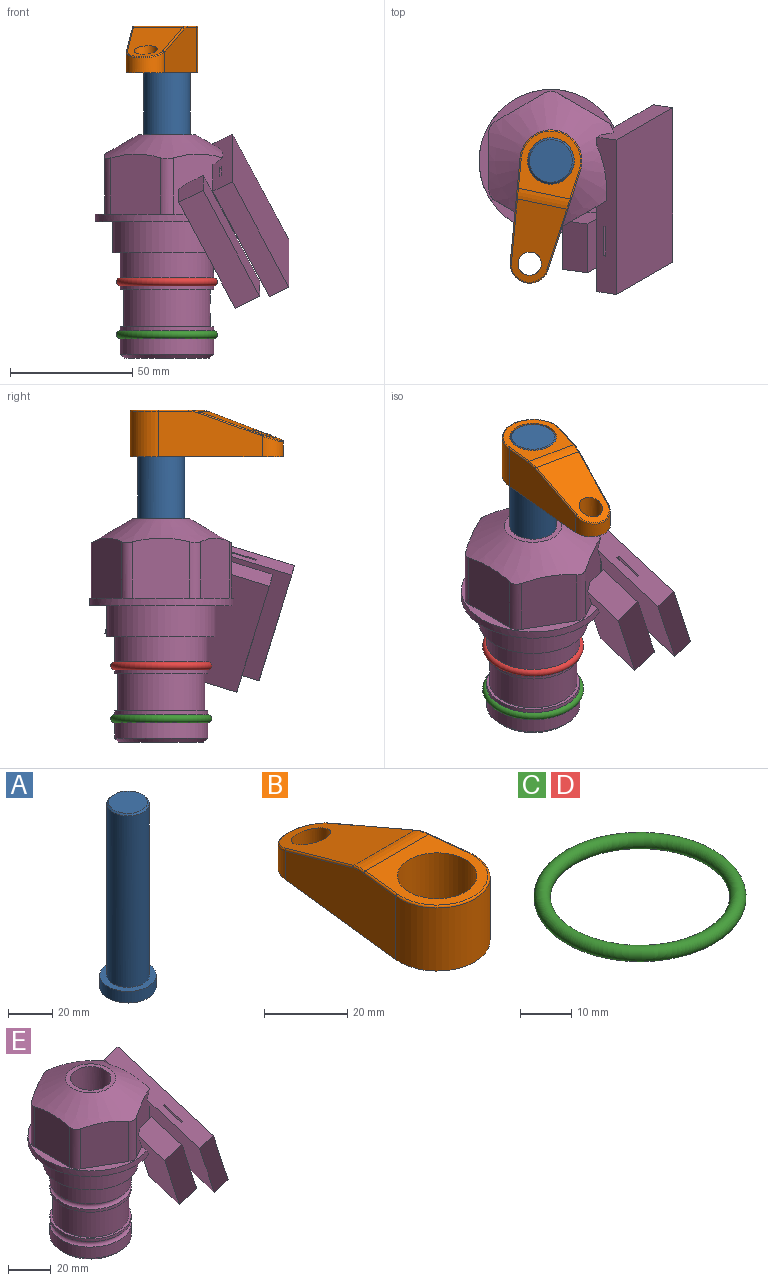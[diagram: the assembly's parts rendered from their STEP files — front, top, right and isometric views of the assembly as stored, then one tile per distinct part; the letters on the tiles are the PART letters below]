
ASSEMBLY  parts=5 mates=3
PART A: 6 faces, bbox 25.4x25.4x101.6 mm
  f0: plane 17.46x17.46mm, normal (0,0,1), area 239.5mm2, adj f5
  f1: plane 25.4x25.4mm, normal (0,0,-1), area 506.7mm2, adj f2
  f2: cylinder r=12.7mm len=25.4mm, axis (0,0,1), area 506.7mm2, adj f1,f3
  f3: plane 25.4x25.4mm, normal (0,0,1), area 221.7mm2, adj f2,f4
  f4: cylinder r=9.53mm len=94.46mm, axis (0,0,1), area 5653mm2, adj f3,f5
  f5: cone r=8.73mm half-angle=45deg, axis (0,0,-1), area 64.4mm2, adj f0,f4
PART B: 44 faces, bbox 27.5x64.5x19.1 mm
  f0: plane 2.3x0.95mm, normal (0,0,-1), area 1mm2, adj f25,f30,f34
  f1: plane 63.5x25.4mm, normal (0,0,-1), area 561.7mm2, adj f2,f3,f4,f5,f6,f7,f19,f20
  f2: cylinder r=12.7mm len=25.4mm, axis (0,0,-1), area 792.2mm2, adj f1,f3,f5,f13
  f3: plane 42.33x18.54mm, normal (0.99,0.11,0), area 647mm2, adj f1,f2,f4,f11,f12,f14
  f4: cylinder r=7.94mm len=15.78mm, axis (0,0,-1), area 158.6mm2, adj f1,f3,f5,f16
  f5: plane 42.33x18.54mm, normal (-0.99,0.11,0), area 647mm2, adj f1,f2,f4,f15,f17,f18
  f6: cylinder r=9.53mm len=19.05mm, axis (0,0,-1), area 1140.1mm2, adj f1,f8
  f7: cylinder r=4.76mm len=10.98mm, axis (0,0,-1), area 276.1mm2, adj f1,f9
  f8: plane 25.83x24.38mm, normal (0,0,1), area 262.2mm2, adj f6,f10,f11,f13,f15
  f9: plane 32.49x20.55mm, normal (0,0.34,0.94), area 489.9mm2, adj f7,f10,f14,f16,f18
  f10: cylinder r=12.7mm len=21.49mm, axis (-1,0,0), area 93.2mm2, adj f8,f9,f12,f17
  f11: cylinder r=0.51mm len=12.34mm, axis (0.11,-0.99,0), area 9.9mm2, adj f3,f8,f12,f13
  f12: bspline ~7.62x1.64mm, area 3.5mm2, adj f3,f10,f11,f14
  f13: torus R=12.19mm, axis (0,0,1), area 33.6mm2, adj f2,f8,f11,f15
  f14: cylinder r=0.51mm len=26.01mm, axis (0.1,-0.93,0.34), area 21.6mm2, adj f3,f9,f12,f16
  f15: cylinder r=0.51mm len=12.34mm, axis (0.11,0.99,0), area 9.9mm2, adj f5,f8,f13,f17
  f16: bspline ~15.78x7.05mm, area 15.7mm2, adj f4,f9,f14,f18
  f17: bspline ~7.62x1.64mm, area 3.5mm2, adj f5,f10,f15,f18
  f18: cylinder r=0.51mm len=26.01mm, axis (0.1,0.93,-0.34), area 21.6mm2, adj f5,f9,f16,f17
  f19: plane 21.6x14.29mm, normal (-0.99,-0.11,0), area 242.6mm2, adj f1,f26,f28,f34,f36,f38
  f20: plane 21.6x14.29mm, normal (0.99,-0.11,0), area 242.6mm2, adj f1,f27,f29,f37,f39,f41
  f21: cylinder r=12.7mm len=14.29mm, axis (0,0,-1), area 173.2mm2, adj f1,f26,f27,f30,f31,f33
  f22: cylinder r=7.94mm len=7.63mm, axis (0,0,-1), area 53.8mm2, adj f1,f28,f29,f42
  f23: plane 2.3x0.95mm, normal (0,0,-1), area 1mm2, adj f25,f33,f37
  f24: plane 17.94x12.32mm, normal (0,-0.34,-0.94), area 191.2mm2, adj f25,f38,f41,f42
  f25: cylinder r=9.53mm len=12.93mm, axis (-1,0,0), area 37.5mm2, adj f0,f23,f24,f31,f36,f39
  f26: cylinder r=1.59mm len=14.29mm, axis (0,0,-1), area 49mm2, adj f1,f19,f21,f32
  f27: cylinder r=1.59mm len=14.29mm, axis (0,0,-1), area 49mm2, adj f1,f20,f21,f35
  f28: cylinder r=1.59mm len=7.28mm, axis (0,0,-1), area 22.1mm2, adj f1,f19,f22,f40
  f29: cylinder r=1.59mm len=7.28mm, axis (0,0,-1), area 22.1mm2, adj f1,f20,f22,f43
  f30: torus R=14.29mm, axis (0,0,1), area 5.8mm2, adj f0,f21,f31,f32
  f31: bspline ~11.06x2.73mm, area 20.8mm2, adj f21,f25,f30,f33
  f32: sphere r=1.59mm, area 5.4mm2, adj f26,f30,f34
  f33: torus R=14.29mm, axis (0,0,1), area 5.8mm2, adj f21,f23,f31,f35
  f34: cylinder r=1.59mm len=1.68mm, axis (-0.11,0.99,0), area 2.4mm2, adj f0,f19,f32,f36
  f35: sphere r=1.59mm, area 5.4mm2, adj f27,f33,f37
  f36: bspline ~5.82x2.33mm, area 7.7mm2, adj f19,f25,f34,f38
  f37: cylinder r=1.59mm len=1.68mm, axis (0.11,0.99,0), area 2.4mm2, adj f20,f23,f35,f39
  f38: cylinder r=1.59mm len=18.33mm, axis (0.1,-0.93,0.34), area 46.7mm2, adj f19,f24,f36,f40
  f39: bspline ~5.82x2.33mm, area 7.7mm2, adj f20,f25,f37,f41
  f40: sphere r=1.59mm, area 3.6mm2, adj f28,f38,f42
  f41: cylinder r=1.59mm len=18.33mm, axis (0.1,0.93,-0.34), area 46.7mm2, adj f20,f24,f39,f43
  f42: bspline ~8.31x1.84mm, area 15.3mm2, adj f22,f24,f40,f43
  f43: sphere r=1.59mm, area 3.6mm2, adj f29,f41,f42
PART C: 1 faces, bbox 44.7x44.7x3.2 mm
  f0: torus R=19.05mm, axis (0,0,1), area 1193.9mm2
PART D: same geometry as C
PART E: 54 faces, bbox 79.4x84.1x91.8 mm
  f0: plane 24.5x20.32mm, normal (0.5,-0.87,0), area 480.9mm2, adj f4,f5,f10,f18,f43,f47,f50,f51
  f1: plane 23.46x15.81mm, normal (1,0,0), area 286.3mm2, adj f3,f4,f10,f43
  f2: plane 0.56x0.17mm, normal (1,0,0), area 0mm2, adj f3,f5,f44
  f3: cylinder r=5.08mm len=23.01mm, axis (0,0,-1), area 115.4mm2, adj f1,f2,f5,f10,f14,f43,f44
  f4: cylinder r=5.08mm len=12.46mm, axis (0,0,-1), area 51.3mm2, adj f0,f1,f10,f43
  f5: cone r=11.73mm half-angle=60deg, axis (0,0,-1), area 1947.2mm2, adj f0,f2,f3,f11,f12,f13,f14,f15
  f6: cylinder r=17.78mm len=35.56mm, axis (0,0,1), area 1670.8mm2, adj f24,f25,f32
  f7: cylinder r=19.05mm len=38.1mm, axis (0,0,1), area 1191.9mm2, adj f27,f28,f31
  f8: plane 58.66x58.66mm, normal (0,0,-1), area 1112.1mm2, adj f9,f29,f50,f51
  f9: cylinder r=29.33mm len=58.66mm, axis (0,0,-1), area 544.4mm2, adj f8,f10,f50,f51
  f10: plane 58.66x58.66mm, normal (0,0,1), area 440.8mm2, adj f0,f1,f3,f4,f9,f11,f12,f13
  f11: plane 24.5x20.32mm, normal (-0.5,-0.87,0), area 562.8mm2, adj f5,f10,f17,f18
  f12: plane 24.5x23.48mm, normal (-1,0,0), area 562.8mm2, adj f5,f10,f16,f17
  f13: plane 24.5x20.32mm, normal (-0.5,0.87,0), area 562.8mm2, adj f5,f10,f15,f16
  f14: plane 24.5x20.32mm, normal (0.5,0.87,0), area 562.8mm2, adj f3,f5,f10,f15
  f15: cylinder r=5.08mm len=23.01mm, axis (0,0,-1), area 121.2mm2, adj f5,f10,f13,f14
  f16: cylinder r=5.08mm len=23.01mm, axis (0,0,-1), area 121.2mm2, adj f5,f10,f12,f13
  f17: cylinder r=5.08mm len=23.01mm, axis (0,0,-1), area 121.2mm2, adj f5,f10,f11,f12
  f18: cylinder r=5.08mm len=23.01mm, axis (0,0,-1), area 121.2mm2, adj f0,f5,f10,f11
  f19: plane 23.46x23.46mm, normal (0,0,1), area 147.4mm2, adj f5,f36
  f20: plane 34.93x34.93mm, normal (0,0,-1), area 958mm2, adj f30
  f21: cylinder r=19.05mm len=38.1mm, axis (0,0,1), area 760.1mm2, adj f22,f30
  f22: torus R=19.05mm, axis (0,0,1), area 565.3mm2, adj f21,f23
  f23: cylinder r=19.05mm len=38.1mm, axis (0,0,1), area 190mm2, adj f22,f24
  f24: plane 38.1x38.1mm, normal (0,0,1), area 146.9mm2, adj f6,f23
  f25: plane 38.1x38.1mm, normal (0,0,-1), area 146.9mm2, adj f6,f26
  f26: cylinder r=19.05mm len=38.1mm, axis (0,0,1), area 190mm2, adj f25,f27
  f27: torus R=19.05mm, axis (0,0,1), area 565.3mm2, adj f7,f26
  f28: plane 44.45x44.45mm, normal (0,0,-1), area 411.7mm2, adj f7,f29
  f29: cylinder r=22.23mm len=44.45mm, axis (0,0,1), area 1773.5mm2, adj f8,f28
  f30: cone r=19.05mm half-angle=45deg, axis (0,0,1), area 257.5mm2, adj f20,f21
  f31: cylinder r=3.17mm len=6.75mm, axis (-1,0,0), area 128mm2, adj f7,f34
  f32: cylinder r=3.17mm len=6.35mm, axis (-1,0,0), area 102.5mm2, adj f6,f34
  f33: plane 25.4x25.4mm, normal (0,0,1), area 506.7mm2, adj f34
  f34: cylinder r=12.7mm len=66.42mm, axis (0,0,-1), area 5236.2mm2, adj f31,f32,f33,f35
  f35: cone r=9.53mm half-angle=30deg, axis (0,0,-1), area 443.4mm2, adj f34,f36
  f36: cylinder r=9.53mm len=19.05mm, axis (0,0,-1), area 849mm2, adj f19,f35
  f37: plane 4.41x2.91mm, normal (-0.89,0.13,-0.43), area 6.1mm2, adj f5,f44,f47
  f38: plane 43.62x23.78mm, normal (0,-0.96,-0.29), area 41.5mm2, adj f39,f45,f46,f47
  f39: plane 46.94x25.23mm, normal (0.89,-0.13,0.43), area 633.5mm2, adj f38,f40,f46,f47
  f40: plane 43.62x23.78mm, normal (0,0.96,0.29), area 41.5mm2, adj f39,f45,f46,f47
  f41: plane 76.38x62.67mm, normal (0.89,-0.13,0.43), area 3352.3mm2, adj f42,f44,f46,f47
  f42: plane 47.15x31.02mm, normal (0,-0.96,-0.29), area 454.3mm2, adj f41,f43,f46,f47
  f43: plane 76.68x54.27mm, normal (-0.89,0.13,-0.43), area 2924.6mm2, adj f0,f1,f3,f4,f42,f44,f46,f47
  f44: plane 47.29x31.17mm, normal (0,0.96,0.29), area 437.3mm2, adj f2,f3,f5,f37,f41,f43,f46,f47
  f45: plane 46.94x25.23mm, normal (-0.89,0.13,-0.43), area 633.5mm2, adj f38,f40,f46,f47
  f46: plane 64.27x23.28mm, normal (0.45,0.26,-0.85), area 580mm2, adj f38,f39,f40,f41,f42,f43,f44,f45
  f47: plane 64.27x23.28mm, normal (-0.45,-0.26,0.85), area 497.6mm2, adj f0,f5,f37,f38,f39,f40,f41,f42
  f48: plane 49.4x33.23mm, normal (0.89,-0.13,0.43), area 1059mm2, adj f49,f51,f52,f53
  f49: plane 48.12x33.02mm, normal (0,-0.96,-0.29), area 568.1mm2, adj f48,f50,f52,f53
  f50: plane 48.72x33.26mm, normal (-0.89,0.13,-0.43), area 1004.1mm2, adj f0,f8,f9,f10,f49,f51,f52,f53
  f51: plane 48.15x29.89mm, normal (0,0.96,0.29), area 487.5mm2, adj f0,f8,f9,f10,f48,f50,f52,f53
  f52: plane 21.42x10.98mm, normal (0.45,0.26,-0.85), area 233.1mm2, adj f48,f49,f50,f51
  f53: plane 20.94x10.98mm, normal (-0.45,-0.26,0.85), area 228.8mm2, adj f0,f48,f49,f50,f51
PLACE A rot(axis=(0,0,-1),101.7deg) t=(0,0,6.38)mm
PLACE B rot(axis=(0,0,1),168.3deg) t=(0,0,60.99)mm
PLACE C t=(0,0,-21.59)mm
PLACE D at identity
PLACE E at identity fixed
MATE fastened C.f0 <-> E.f5  axis (0,0,1) through (0,0,-46.1)mm
MATE cylindrical A.f2 <-> E.f5  axis (0,0,1) through (0,0,32.01)mm
MATE fastened B.f2 <-> A.f2  axis (0,0,1) through (0,0,80.04)mm
